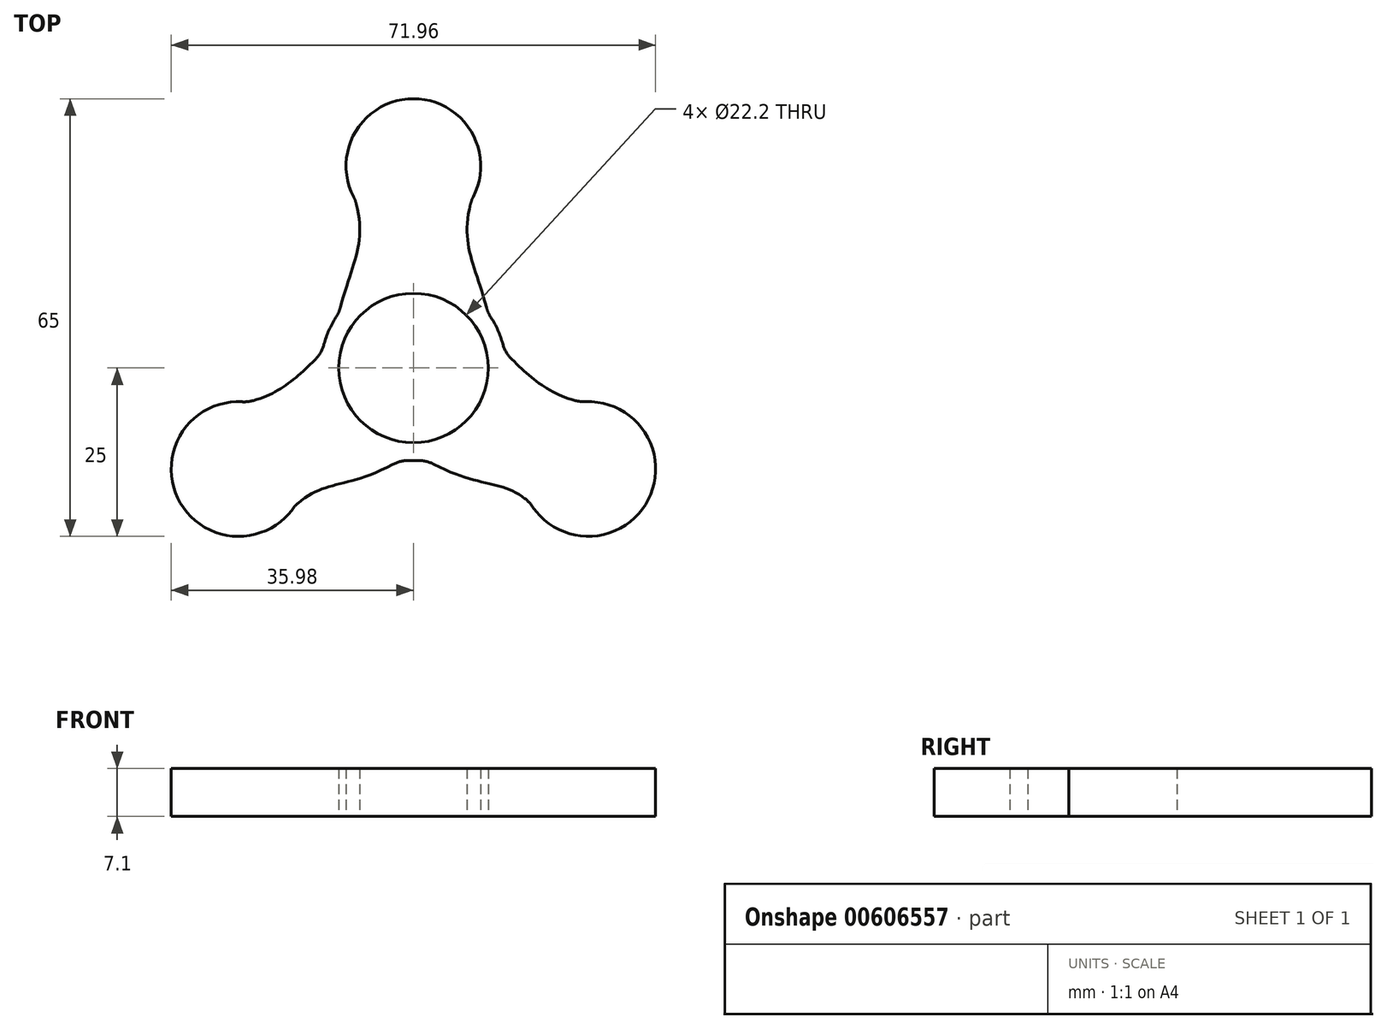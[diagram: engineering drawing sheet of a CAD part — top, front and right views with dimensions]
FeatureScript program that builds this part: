
annotation { "Feature Type Name" : "Feature", "Feature Type Description" : "" }
export const myFeature = defineFeature(function(context is Context, id is Id, definition is map)
    precondition{}
    {
        {
            var Q0;
            Q0=qCreatedBy(makeId("Top.planeOp"),FACE);
            var sketch = newSketch(context, id + "F0", { "sketchPlane" : qUnion([Q0])});
            skCircle(sketch, "E0", {"center": v(0, 0) * mm, "radius": 11.1 * mm});
            skCircle(sketch, "E1", {"center": v(0, 0) * mm, "radius": 12.5 * mm, "construction": true});
            skLineSegment(sketch, "E2", {"start": v(0, 0) * mm, "end": v(0, 30) * mm, "construction": true});
            skLineSegment(sketch, "E3", {"start": v(0, 0) * mm, "end": v(-25.98, -15) * mm, "construction": true});
            skLineSegment(sketch, "E4", {"start": v(0, 0) * mm, "end": v(25.98, -15) * mm, "construction": true});
            skCircle(sketch, "E5", {"center": v(-25.98, -15) * mm, "radius": 10 * mm});
            skCircle(sketch, "E6", {"center": v(0, 30) * mm, "radius": 10 * mm});
            skCircle(sketch, "E7", {"center": v(25.98, -15) * mm, "radius": 10 * mm});
            skCircle(sketch, "E8", {"center": v(0, 0) * mm, "radius": 30 * mm, "construction": true});
            skFitSpline(sketch, "E9", {"points": [v(-9.86, 28.33) * mm, v(-12.5, 0) * mm], "startDerivative": vector(14.58, -34.66) * mm, "endDerivative": vector(-5.1, -48.44) * mm});
            skFitSpline(sketch, "E10", {"points": [v(9.86, 28.33) * mm, v(12.5, 0) * mm], "startDerivative": vector(-14.58, -34.66) * mm, "endDerivative": vector(5.1, -48.44) * mm});
            skFitSpline(sketch, "E11", {"points": [v(0, 12.5) * mm, v(-29.47, -5.63) * mm], "startDerivative": vector(-49.26, -26.05) * mm, "endDerivative": vector(-42.84, -1.25) * mm});
            skFitSpline(sketch, "E12", {"points": [v(0, -12.5) * mm, v(-19.6, -22.7) * mm], "startDerivative": vector(-32.03, -20.9) * mm, "endDerivative": vector(-18.13, -22.89) * mm});
            skFitSpline(sketch, "E13", {"points": [v(0, -12.5) * mm, v(19.6, -22.7) * mm], "startDerivative": vector(32.03, -20.9) * mm, "endDerivative": vector(16.68, -23.45) * mm});
            skFitSpline(sketch, "E14", {"points": [v(0, 12.5) * mm, v(29.47, -5.63) * mm], "startDerivative": vector(49.26, -26.05) * mm, "endDerivative": vector(43.1, -2.05) * mm});
            skCircle(sketch, "E15", {"center": v(0, 0) * mm, "radius": 13.75 * mm});
            skSolve(sketch);
        }
        {
            var Q0;
            Q0=makeQuery(id+"F0.imprint","IMPRINT",FACE,{"disambiguationData":[TD([[makeQuery(id+"F0.imprint","IMPRINT",EDGE,{"derivedFrom":sQuery(id+"F0.wireOp",EDGE,"E0")}),-1.0]])]});
            var Q1;
            {var subQ0=sQuery(id+"F0.wireOp",EDGE,"E15");var subQ1=sQuery(id+"F0.wireOp",EDGE,"E9");var subQ2=makeQuery(id+"F0.imprint","INTERSECT",VERTEX,{"derivedFrom":[subQ1,subQ0]});Q1=makeQuery(id+"F0.imprint","IMPRINT",FACE,{"disambiguationData":[TD([[makeQuery(id+"F0.imprint","IMPRINT",EDGE,{"disambiguationData":[TD([[subQ2,-1.0]])],"derivedFrom":subQ1}),-1.0]])]});}
            var Q2;
            {var subQ5=sQuery(id+"F0.wireOp",EDGE,"E15");var subQ7=sQuery(id+"F0.wireOp",EDGE,"E9");var subQ9=makeQuery(id+"F0.imprint","INTERSECT",VERTEX,{"derivedFrom":[subQ7,subQ5]});Q2=makeQuery(id+"F0.imprint","IMPRINT",FACE,{"disambiguationData":[TD([[makeQuery(id+"F0.imprint","IMPRINT",EDGE,{"disambiguationData":[TD([[subQ9,-1.0]])],"derivedFrom":subQ7}),1.0]])]});}
            var Q3;
            {var subQ0=sQuery(id+"F0.wireOp",EDGE,"E15");var subQ1=sQuery(id+"F0.wireOp",EDGE,"E10");var subQ2=makeQuery(id+"F0.imprint","INTERSECT",VERTEX,{"derivedFrom":[subQ1,subQ0]});Q3=makeQuery(id+"F0.imprint","IMPRINT",FACE,{"disambiguationData":[TD([[makeQuery(id+"F0.imprint","IMPRINT",EDGE,{"disambiguationData":[TD([[subQ2,-1.0]])],"derivedFrom":subQ1}),1.0]])]});}
            var Q4;
            {var subQ0=sQuery(id+"F0.wireOp",EDGE,"E11");var subQ1=sQuery(id+"F0.wireOp",EDGE,"E5");var subQ2=makeQuery(id+"F0.imprint","INTERSECT",VERTEX,{"disambiguationData":[OD(1.0)],"derivedFrom":[subQ1,subQ0]});Q4=makeQuery(id+"F0.imprint","IMPRINT",FACE,{"disambiguationData":[TD([[makeQuery(id+"F0.imprint","IMPRINT",EDGE,{"disambiguationData":[TD([[subQ2,1.0]])],"derivedFrom":subQ1}),-1.0]])]});}
            var Q5;
            {var subQ0=sQuery(id+"F0.wireOp",EDGE,"E14");var subQ1=sQuery(id+"F0.wireOp",EDGE,"E7");var subQ2=makeQuery(id+"F0.imprint","INTERSECT",VERTEX,{"disambiguationData":[OD(1.0)],"derivedFrom":[subQ1,subQ0]});Q5=makeQuery(id+"F0.imprint","IMPRINT",FACE,{"disambiguationData":[TD([[makeQuery(id+"F0.imprint","IMPRINT",EDGE,{"disambiguationData":[TD([[subQ2,-1.0]])],"derivedFrom":subQ1}),-1.0]])]});}
            var Q6;
            {var subQ0=sQuery(id+"F0.wireOp",EDGE,"E14");var subQ1=sQuery(id+"F0.wireOp",EDGE,"E7");var subQ2=makeQuery(id+"F0.imprint","INTERSECT",VERTEX,{"disambiguationData":[OD(1.0)],"derivedFrom":[subQ1,subQ0]});Q6=makeQuery(id+"F0.imprint","IMPRINT",FACE,{"disambiguationData":[TD([[makeQuery(id+"F0.imprint","IMPRINT",EDGE,{"disambiguationData":[TD([[subQ2,-1.0]])],"derivedFrom":subQ1}),1.0]])]});}
            var Q7;
            {var subQ0=sQuery(id+"F0.wireOp",EDGE,"E9");var subQ1=sQuery(id+"F0.wireOp",EDGE,"E6");var subQ2=makeQuery(id+"F0.imprint","INTERSECT",VERTEX,{"disambiguationData":[OD(1.0)],"derivedFrom":[subQ1,subQ0]});Q7=makeQuery(id+"F0.imprint","IMPRINT",FACE,{"disambiguationData":[TD([[makeQuery(id+"F0.imprint","IMPRINT",EDGE,{"disambiguationData":[TD([[subQ2,-1.0]])],"derivedFrom":subQ1}),-1.0]])]});}
            var Q8;
            {var subQ0=sQuery(id+"F0.wireOp",EDGE,"E9");var subQ1=sQuery(id+"F0.wireOp",EDGE,"E6");var subQ2=makeQuery(id+"F0.imprint","INTERSECT",VERTEX,{"disambiguationData":[OD(1.0)],"derivedFrom":[subQ1,subQ0]});Q8=makeQuery(id+"F0.imprint","IMPRINT",FACE,{"disambiguationData":[TD([[makeQuery(id+"F0.imprint","IMPRINT",EDGE,{"disambiguationData":[TD([[subQ2,-1.0]])],"derivedFrom":subQ1}),1.0]])]});}
            var Q9;
            {var subQ0=sQuery(id+"F0.wireOp",EDGE,"E11");var subQ1=sQuery(id+"F0.wireOp",EDGE,"E5");var subQ2=makeQuery(id+"F0.imprint","INTERSECT",VERTEX,{"disambiguationData":[OD(0.0)],"derivedFrom":[subQ1,subQ0]});Q9=makeQuery(id+"F0.imprint","IMPRINT",FACE,{"disambiguationData":[TD([[makeQuery(id+"F0.imprint","IMPRINT",EDGE,{"disambiguationData":[TD([[subQ2,-1.0]])],"derivedFrom":subQ1}),1.0]])]});}
            var Q10;
            {var subQ0=sQuery(id+"F0.wireOp",EDGE,"E9");var subQ1=sQuery(id+"F0.wireOp",EDGE,"E6");var subQ2=makeQuery(id+"F0.imprint","INTERSECT",VERTEX,{"disambiguationData":[OD(0.0)],"derivedFrom":[subQ1,subQ0]});Q10=makeQuery(id+"F0.imprint","IMPRINT",FACE,{"disambiguationData":[TD([[makeQuery(id+"F0.imprint","IMPRINT",EDGE,{"disambiguationData":[TD([[subQ2,-1.0]])],"derivedFrom":subQ1}),1.0]])]});}
            var Q11;
            {var subQ0=sQuery(id+"F0.wireOp",EDGE,"E10");var subQ1=sQuery(id+"F0.wireOp",EDGE,"E6");var subQ2=makeQuery(id+"F0.imprint","INTERSECT",VERTEX,{"disambiguationData":[OD(0.0)],"derivedFrom":[subQ1,subQ0]});Q11=makeQuery(id+"F0.imprint","IMPRINT",FACE,{"disambiguationData":[TD([[makeQuery(id+"F0.imprint","IMPRINT",EDGE,{"disambiguationData":[TD([[subQ2,1.0]])],"derivedFrom":subQ1}),1.0]])]});}
            var Q12;
            {var subQ0=sQuery(id+"F0.wireOp",EDGE,"E14");var subQ1=sQuery(id+"F0.wireOp",EDGE,"E7");var subQ2=makeQuery(id+"F0.imprint","INTERSECT",VERTEX,{"disambiguationData":[OD(0.0)],"derivedFrom":[subQ1,subQ0]});Q12=makeQuery(id+"F0.imprint","IMPRINT",FACE,{"disambiguationData":[TD([[makeQuery(id+"F0.imprint","IMPRINT",EDGE,{"disambiguationData":[TD([[subQ2,-1.0]])],"derivedFrom":subQ1}),1.0]])]});}
            var Q13;
            {var subQ0=sQuery(id+"F0.wireOp",EDGE,"E13");var subQ1=sQuery(id+"F0.wireOp",EDGE,"E7");var subQ2=makeQuery(id+"F0.imprint","INTERSECT",VERTEX,{"disambiguationData":[OD(0.0)],"derivedFrom":[subQ1,subQ0]});Q13=makeQuery(id+"F0.imprint","IMPRINT",FACE,{"disambiguationData":[TD([[makeQuery(id+"F0.imprint","IMPRINT",EDGE,{"disambiguationData":[TD([[subQ2,1.0]])],"derivedFrom":subQ1}),1.0]])]});}
            var Q14;
            {var subQ0=sQuery(id+"F0.wireOp",EDGE,"E12");var subQ1=sQuery(id+"F0.wireOp",EDGE,"E5");var subQ2=makeQuery(id+"F0.imprint","INTERSECT",VERTEX,{"disambiguationData":[OD(0.0)],"derivedFrom":[subQ1,subQ0]});Q14=makeQuery(id+"F0.imprint","IMPRINT",FACE,{"disambiguationData":[TD([[makeQuery(id+"F0.imprint","IMPRINT",EDGE,{"disambiguationData":[TD([[subQ2,-1.0]])],"derivedFrom":subQ1}),1.0]])]});}
            var Q15;
            {var subQ0=sQuery(id+"F0.wireOp",EDGE,"E11");var subQ1=sQuery(id+"F0.wireOp",EDGE,"E5");var subQ2=makeQuery(id+"F0.imprint","INTERSECT",VERTEX,{"disambiguationData":[OD(0.0)],"derivedFrom":[subQ1,subQ0]});Q15=makeQuery(id+"F0.imprint","IMPRINT",FACE,{"disambiguationData":[TD([[makeQuery(id+"F0.imprint","IMPRINT",EDGE,{"disambiguationData":[TD([[subQ2,1.0]])],"derivedFrom":subQ1}),1.0]])]});}
            var Q16;
            {var subQ0=sQuery(id+"F0.wireOp",EDGE,"E13");var subQ1=sQuery(id+"F0.wireOp",EDGE,"E12");var subQ2=makeQuery(id+"F0.imprint","INTERSECT",VERTEX,{"derivedFrom":[subQ1,subQ0]});Q16=makeQuery(id+"F0.imprint","IMPRINT",FACE,{"disambiguationData":[TD([[makeQuery(id+"F0.imprint","IMPRINT",EDGE,{"disambiguationData":[TD([[subQ2,-1.0]])],"derivedFrom":subQ1}),1.0]])]});}
            var Q17;
            {var subQ8=sQuery(id+"F0.wireOp",EDGE,"E14");var subQ11=sQuery(id+"F0.wireOp",EDGE,"E0");var subQ13=makeQuery(id+"F0.imprint","INTERSECT",VERTEX,{"disambiguationData":[OD(1.0)],"derivedFrom":[subQ11,subQ8]});Q17=makeQuery(id+"F0.imprint","IMPRINT",FACE,{"disambiguationData":[TD([[makeQuery(id+"F0.imprint","IMPRINT",EDGE,{"disambiguationData":[TD([[subQ13,1.0]])],"derivedFrom":subQ11}),-1.0]])]});}
            var Q18;
            {var subQ0=sQuery(id+"F0.wireOp",EDGE,"E14");var subQ1=sQuery(id+"F0.wireOp",EDGE,"E0");var subQ2=makeQuery(id+"F0.imprint","INTERSECT",VERTEX,{"disambiguationData":[OD(0.0)],"derivedFrom":[subQ1,subQ0]});Q18=makeQuery(id+"F0.imprint","IMPRINT",FACE,{"disambiguationData":[TD([[makeQuery(id+"F0.imprint","IMPRINT",EDGE,{"disambiguationData":[TD([[subQ2,-1.0]])],"derivedFrom":subQ1}),-1.0]])]});}
            extrude(context, id + "F1", {"entities" : qUnion([Q0, Q1, Q2, Q3, Q4, Q5, Q6, Q7, Q8, Q9, Q10, Q11, Q12, Q13, Q14, Q15, Q16, Q17, Q18]), "depth" : 7.1 * mm, "offsetDistance" : 25 * mm});
        }
        {
            var Q0;
            Q0=makeQuery(id+"F1.opExtrude","SWEPT_EDGE",EDGE,{"disambiguationData":[OSD([sQuery(id+"F0.wireOp",EDGE,"E5"),sQuery(id+"F0.wireOp",EDGE,"E12")])]});
            var Q1;
            Q1=makeQuery(id+"F1.opExtrude","SWEPT_EDGE",EDGE,{"disambiguationData":[OSD([sQuery(id+"F0.wireOp",EDGE,"E5"),sQuery(id+"F0.wireOp",EDGE,"E11")])]});
            var Q2;
            Q2=makeQuery(id+"F1.opExtrude","SWEPT_EDGE",EDGE,{"disambiguationData":[OSD([sQuery(id+"F0.wireOp",EDGE,"E7"),sQuery(id+"F0.wireOp",EDGE,"E14")])]});
            var Q3;
            Q3=makeQuery(id+"F1.opExtrude","SWEPT_EDGE",EDGE,{"disambiguationData":[OSD([sQuery(id+"F0.wireOp",EDGE,"E7"),sQuery(id+"F0.wireOp",EDGE,"E13")])]});
            var Q4;
            Q4=makeQuery(id+"F1.opExtrude","SWEPT_EDGE",EDGE,{"disambiguationData":[OSD([sQuery(id+"F0.wireOp",EDGE,"E6"),sQuery(id+"F0.wireOp",EDGE,"E10")])]});
            var Q5;
            Q5=makeQuery(id+"F1.opExtrude","SWEPT_EDGE",EDGE,{"disambiguationData":[OSD([sQuery(id+"F0.wireOp",EDGE,"E6"),sQuery(id+"F0.wireOp",EDGE,"E9")])]});
            var Q6;
            Q6=makeQuery(id+"F1.opExtrude","SWEPT_EDGE",EDGE,{"disambiguationData":[OSD([sQuery(id+"F0.wireOp",EDGE,"E9"),sQuery(id+"F0.wireOp",EDGE,"E15")])]});
            var Q7;
            Q7=makeQuery(id+"F1.opExtrude","SWEPT_EDGE",EDGE,{"disambiguationData":[OSD([sQuery(id+"F0.wireOp",EDGE,"E11"),sQuery(id+"F0.wireOp",EDGE,"E15")])]});
            var Q8;
            Q8=makeQuery(id+"F1.opExtrude","SWEPT_EDGE",EDGE,{"disambiguationData":[OSD([sQuery(id+"F0.wireOp",EDGE,"E10"),sQuery(id+"F0.wireOp",EDGE,"E15")])]});
            var Q9;
            Q9=makeQuery(id+"F1.opExtrude","SWEPT_EDGE",EDGE,{"disambiguationData":[OSD([sQuery(id+"F0.wireOp",EDGE,"E14"),sQuery(id+"F0.wireOp",EDGE,"E15")])]});
            var Q10;
            Q10=makeQuery(id+"F1.opExtrude","SWEPT_EDGE",EDGE,{"disambiguationData":[OSD([sQuery(id+"F0.wireOp",EDGE,"E13"),sQuery(id+"F0.wireOp",EDGE,"E15")])]});
            var Q11;
            Q11=makeQuery(id+"F1.opExtrude","SWEPT_EDGE",EDGE,{"disambiguationData":[OSD([sQuery(id+"F0.wireOp",EDGE,"E12"),sQuery(id+"F0.wireOp",EDGE,"E15")])]});
            fillet(context, id + "F2", {"entities" : qUnion([Q0, Q1, Q2, Q3, Q4, Q5, Q6, Q7, Q8, Q9, Q10, Q11]), "radius" : 5 * mm, "tangentPropagation" : true, "allowEdgeOverflow" : false});
        }
    });
